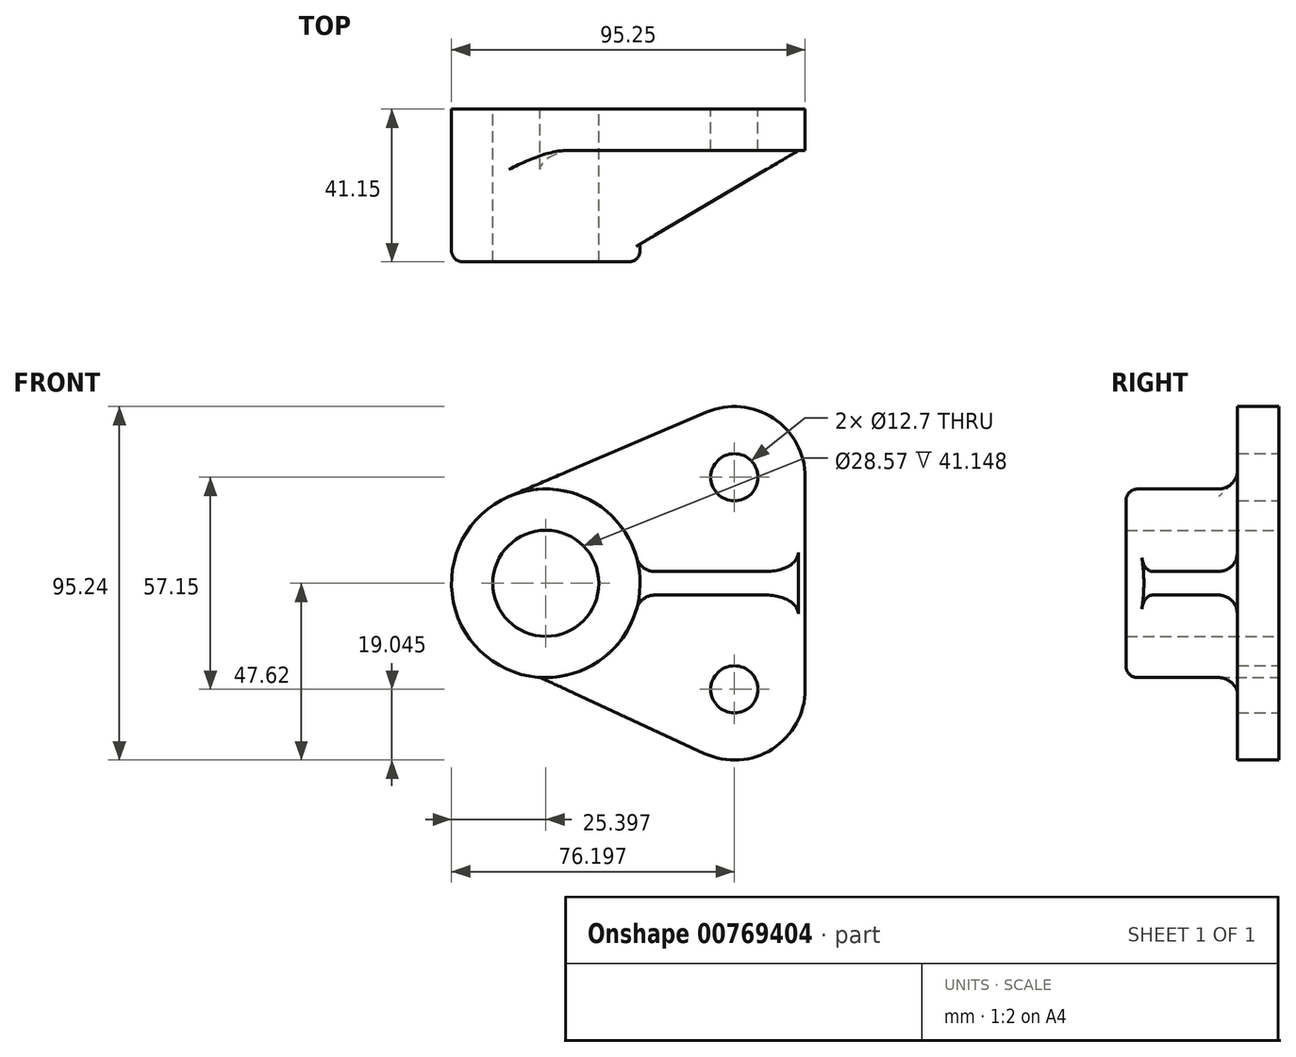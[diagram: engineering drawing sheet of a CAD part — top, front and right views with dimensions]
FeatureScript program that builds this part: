
annotation { "Feature Type Name" : "Feature", "Feature Type Description" : "" }
export const myFeature = defineFeature(function(context is Context, id is Id, definition is map)
    precondition{}
    {
        {
            var Q0;
            Q0=qCreatedBy(makeId("Front.planeOp"),FACE);
            var sketch = newSketch(context, id + "F0", { "sketchPlane" : qUnion([Q0])});
            skCircle(sketch, "E0", {"center": v(1.59, 0) * mm, "radius": 14.29 * mm});
            skCircle(sketch, "E1", {"center": v(1.59, 0) * mm, "radius": 25.4 * mm});
            skLineSegment(sketch, "E2", {"start": v(1.59, 0) * mm, "end": v(52.39, 0) * mm, "construction": true});
            skLineSegment(sketch, "E3", {"start": v(52.39, 0) * mm, "end": v(52.39, -28.57) * mm, "construction": true});
            skLineSegment(sketch, "E4", {"start": v(52.39, 0) * mm, "end": v(52.39, 28.57) * mm, "construction": true});
            skCircle(sketch, "E5", {"center": v(52.39, -28.57) * mm, "radius": 6.35 * mm});
            skCircle(sketch, "E6", {"center": v(52.39, 28.57) * mm, "radius": 6.35 * mm});
            skCircle(sketch, "E7", {"center": v(52.39, 28.57) * mm, "radius": 19.05 * mm});
            skCircle(sketch, "E8", {"center": v(52.39, -28.57) * mm, "radius": 19.05 * mm});
            skLineSegment(sketch, "E9", {"start": v(0, -25.35) * mm, "end": v(44.4, -45.87) * mm});
            skLineSegment(sketch, "E10", {"start": v(-8.38, 23.36) * mm, "end": v(44.91, 46.1) * mm});
            skLineSegment(sketch, "E11", {"start": v(71.44, 28.58) * mm, "end": v(71.44, -28.57) * mm});
            skSolve(sketch);
        }
        {
            var Q0;
            Q0=makeQuery(id+"F0.imprint","IMPRINT",FACE,{"disambiguationData":[TD([[makeQuery(id+"F0.imprint","IMPRINT",EDGE,{"derivedFrom":sQuery(id+"F0.wireOp",EDGE,"E0")}),-1.0]])]});
            extrude(context, id + "F1", {"entities" : qUnion([Q0]), "depth" : 41.15 * mm, "offsetDistance" : 25.4 * mm});
        }
        {
            var Q0;
            Q0 = qSketchRegion(id + "F0", true);
            extrude(context, id + "F2", {"entities" : qUnion([Q0]), "operationType" : NewBodyOperationType.ADD, "depth" : 11.18 * mm, "offsetDistance" : 25.4 * mm});
        }
        {
            var Q0;
            Q0=qCreatedBy(makeId("Top.planeOp"),FACE);
            var sketch = newSketch(context, id + "F3", { "sketchPlane" : qUnion([Q0])});
            skLineSegment(sketch, "E12", {"start": v(8.87, -47.05) * mm, "end": v(85.99, -1.5) * mm});
            skLineSegment(sketch, "E13", {"start": v(85.99, -1.5) * mm, "end": v(19.33, -3.17) * mm});
            skLineSegment(sketch, "E14", {"start": v(19.33, -3.17) * mm, "end": v(20.5, -50.05) * mm});
            skSolve(sketch);
        }
        {
            var Q0;
            {var subQ0=sQuery(id+"F3.wireOp",EDGE,"E13");Q0=makeQuery(id+"F3.imprint","IMPRINT",FACE,{"disambiguationData":[TD([[makeQuery(id+"F3.imprint","IMPRINT",EDGE,{"derivedFrom":subQ0}),1.0]])]});}
            extrude(context, id + "F4", {"entities" : qUnion([Q0]), "operationType" : NewBodyOperationType.ADD, "endBound" : BoundingType.SYMMETRIC, "depth" : 6.35 * mm, "offsetDistance" : 25.4 * mm});
        }
        {
            var Q0;
            {var subQ0=sQuery(id+"F3.wireOp",EDGE,"E12");var subQ1=sQuery(id+"F3.wireOp",EDGE,"E13");Q0=makeQuery(id+"F4.boolean.opBoolean","SPLIT",FACE,{"disambiguationData":[TD([makeQuery(id+"F2.opExtrude","SWEPT_FACE",FACE,{"disambiguationData":[OSD([sQuery(id+"F0.wireOp",EDGE,"E11")])]})])],"derivedFrom":makeQuery(id+"F4.opExtrude","CAP_FACE",FACE,{"disambiguationData":[OSD([subQ0,subQ1,sQuery(id+"F3.wireOp",EDGE,"E14")])],"isStart":true})});}
            extrude(context, id + "F5", {"entities" : qUnion([Q0]), "operationType" : NewBodyOperationType.REMOVE, "oppositeDirection" : true, "depth" : 25.4 * mm, "offsetDistance" : 25.4 * mm});
        }
        {
            var Q0;
            {var subQ0=sQuery(id+"F0.wireOp",EDGE,"E1");var subQ1=makeQuery(id+"F1.opExtrude","SWEPT_FACE",FACE,{"disambiguationData":[OSD([subQ0])]});var subQ2=sQuery(id+"F0.wireOp",EDGE,"E9");var subQ3=makeQuery(id+"F2.opExtrude","CAP_FACE",FACE,{"disambiguationData":[OSD([sQuery(id+"F0.wireOp",EDGE,"E0"),subQ0,sQuery(id+"F0.wireOp",EDGE,"E5"),sQuery(id+"F0.wireOp",EDGE,"E6"),sQuery(id+"F0.wireOp",EDGE,"E7"),sQuery(id+"F0.wireOp",EDGE,"E8"),subQ2,sQuery(id+"F0.wireOp",EDGE,"E10"),sQuery(id+"F0.wireOp",EDGE,"E11")])],"isStart":false});Q0=makeQuery(id+"F4.boolean.opBoolean","SPLIT",EDGE,{"disambiguationData":[TD([makeQuery(id+"F2.opExtrude","SWEPT_FACE",FACE,{"disambiguationData":[OSD([subQ2])]})])],"derivedFrom":makeQuery(id+"F2.boolean.opBoolean","INTERSECT",EDGE,{"derivedFrom":[subQ1,subQ3]})});}
            var Q1;
            Q1=makeQuery(id+"F4.boolean.opBoolean","INTERSECT",EDGE,{"derivedFrom":[makeQuery(id+"F1.opExtrude","SWEPT_FACE",FACE,{"disambiguationData":[OSD([sQuery(id+"F0.wireOp",EDGE,"E1")])]}),makeQuery(id+"F4.opExtrude","CAP_FACE",FACE,{"disambiguationData":[OSD([sQuery(id+"F3.wireOp",EDGE,"E12"),sQuery(id+"F3.wireOp",EDGE,"E13"),sQuery(id+"F3.wireOp",EDGE,"E14")])],"isStart":true})]});
            var Q2;
            Q2=makeQuery(id+"F4.boolean.opBoolean","INTERSECT",EDGE,{"derivedFrom":[makeQuery(id+"F2.opExtrude","CAP_FACE",FACE,{"disambiguationData":[OSD([sQuery(id+"F0.wireOp",EDGE,"E0"),sQuery(id+"F0.wireOp",EDGE,"E1"),sQuery(id+"F0.wireOp",EDGE,"E5"),sQuery(id+"F0.wireOp",EDGE,"E6"),sQuery(id+"F0.wireOp",EDGE,"E7"),sQuery(id+"F0.wireOp",EDGE,"E8"),sQuery(id+"F0.wireOp",EDGE,"E9"),sQuery(id+"F0.wireOp",EDGE,"E10"),sQuery(id+"F0.wireOp",EDGE,"E11")])],"isStart":false}),makeQuery(id+"F4.opExtrude","CAP_FACE",FACE,{"disambiguationData":[OSD([sQuery(id+"F3.wireOp",EDGE,"E12"),sQuery(id+"F3.wireOp",EDGE,"E13"),sQuery(id+"F3.wireOp",EDGE,"E14")])],"isStart":true})]});
            var Q3;
            {var subQ0=sQuery(id+"F0.wireOp",EDGE,"E1");var subQ1=makeQuery(id+"F1.opExtrude","SWEPT_FACE",FACE,{"disambiguationData":[OSD([subQ0])]});var subQ2=sQuery(id+"F0.wireOp",EDGE,"E10");var subQ3=makeQuery(id+"F2.opExtrude","CAP_FACE",FACE,{"disambiguationData":[OSD([sQuery(id+"F0.wireOp",EDGE,"E0"),subQ0,sQuery(id+"F0.wireOp",EDGE,"E5"),sQuery(id+"F0.wireOp",EDGE,"E6"),sQuery(id+"F0.wireOp",EDGE,"E7"),sQuery(id+"F0.wireOp",EDGE,"E8"),sQuery(id+"F0.wireOp",EDGE,"E9"),subQ2,sQuery(id+"F0.wireOp",EDGE,"E11")])],"isStart":false});Q3=makeQuery(id+"F4.boolean.opBoolean","SPLIT",EDGE,{"disambiguationData":[TD([makeQuery(id+"F2.opExtrude","SWEPT_FACE",FACE,{"disambiguationData":[OSD([subQ2])]})])],"derivedFrom":makeQuery(id+"F2.boolean.opBoolean","INTERSECT",EDGE,{"derivedFrom":[subQ1,subQ3]})});}
            var Q4;
            Q4=makeQuery(id+"F4.boolean.opBoolean","INTERSECT",EDGE,{"derivedFrom":[makeQuery(id+"F2.opExtrude","CAP_FACE",FACE,{"disambiguationData":[OSD([sQuery(id+"F0.wireOp",EDGE,"E0"),sQuery(id+"F0.wireOp",EDGE,"E1"),sQuery(id+"F0.wireOp",EDGE,"E5"),sQuery(id+"F0.wireOp",EDGE,"E6"),sQuery(id+"F0.wireOp",EDGE,"E7"),sQuery(id+"F0.wireOp",EDGE,"E8"),sQuery(id+"F0.wireOp",EDGE,"E9"),sQuery(id+"F0.wireOp",EDGE,"E10"),sQuery(id+"F0.wireOp",EDGE,"E11")])],"isStart":false}),makeQuery(id+"F4.opExtrude","CAP_FACE",FACE,{"disambiguationData":[OSD([sQuery(id+"F3.wireOp",EDGE,"E12"),sQuery(id+"F3.wireOp",EDGE,"E13"),sQuery(id+"F3.wireOp",EDGE,"E14")])],"isStart":false})]});
            var Q5;
            Q5=makeQuery(id+"F4.boolean.opBoolean","INTERSECT",EDGE,{"derivedFrom":[makeQuery(id+"F1.opExtrude","SWEPT_FACE",FACE,{"disambiguationData":[OSD([sQuery(id+"F0.wireOp",EDGE,"E1")])]}),makeQuery(id+"F4.opExtrude","CAP_FACE",FACE,{"disambiguationData":[OSD([sQuery(id+"F3.wireOp",EDGE,"E12"),sQuery(id+"F3.wireOp",EDGE,"E13"),sQuery(id+"F3.wireOp",EDGE,"E14")])],"isStart":false})]});
            fillet(context, id + "F6", {"entities" : qUnion([Q0, Q1, Q2, Q3, Q4, Q5]), "radius" : 5.08 * mm, "tangentPropagation" : true, "allowEdgeOverflow" : false});
        }
        {
            var Q0;
            Q0=makeQuery(id+"F1.opExtrude","CAP_EDGE",EDGE,{"disambiguationData":[OSD([sQuery(id+"F0.wireOp",EDGE,"E1")])],"isStart":false});
            fillet(context, id + "F7", {"entities" : qUnion([Q0]), "radius" : 3.05 * mm, "tangentPropagation" : true, "allowEdgeOverflow" : false});
        }
    });
